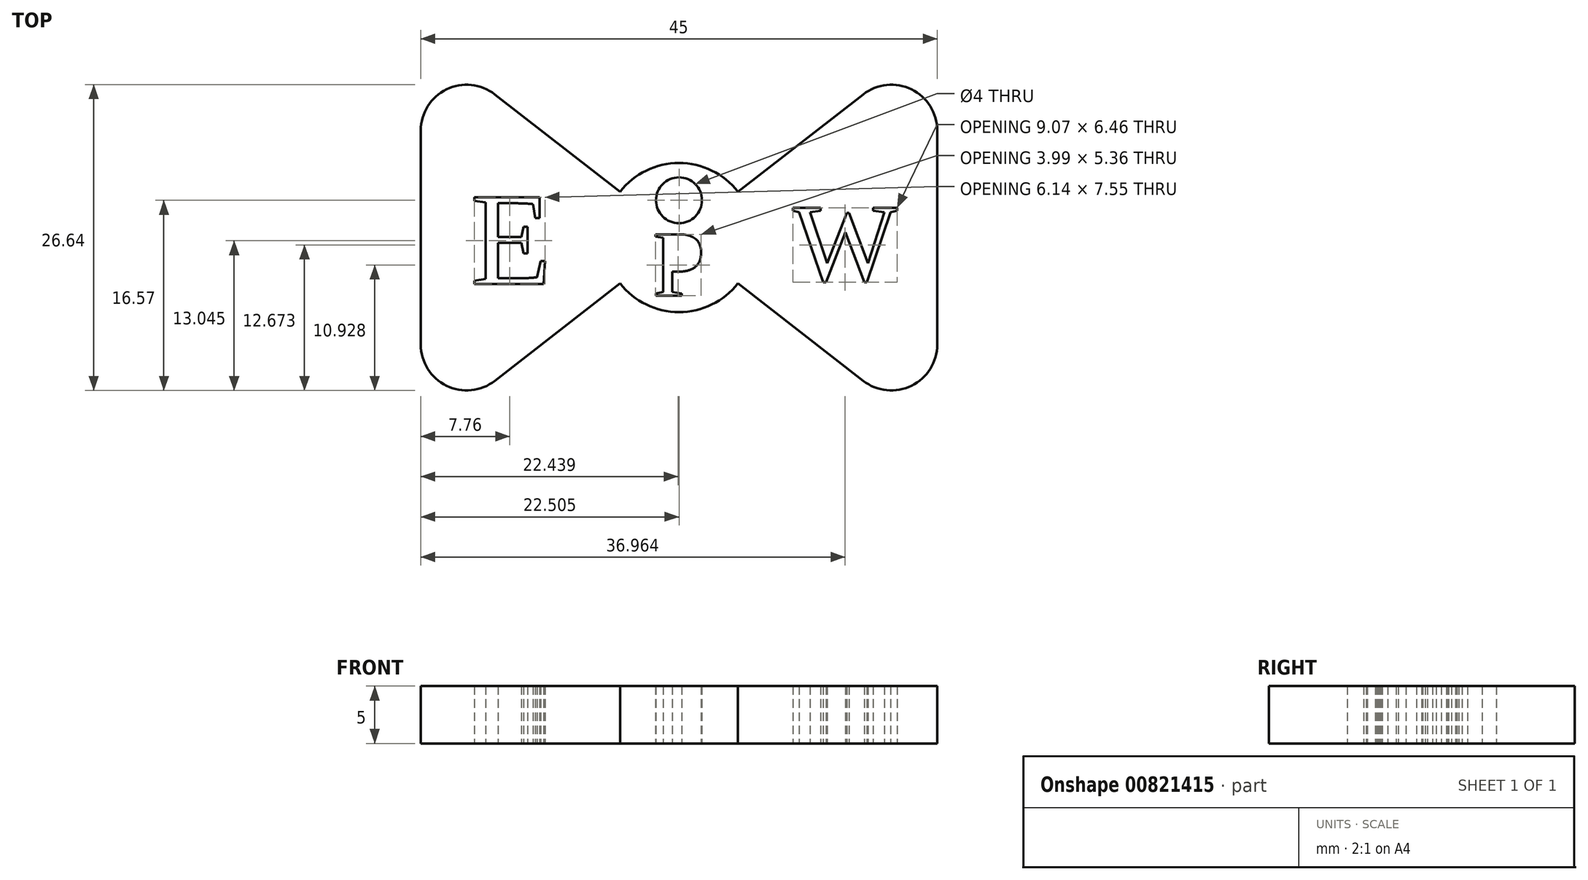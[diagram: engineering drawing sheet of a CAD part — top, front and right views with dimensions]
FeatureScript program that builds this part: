
annotation { "Feature Type Name" : "Feature", "Feature Type Description" : "" }
export const myFeature = defineFeature(function(context is Context, id is Id, definition is map)
    precondition{}
    {
        {
            var Q0;
            Q0=qCreatedBy(makeId("Top.planeOp"),FACE);
            var sketch = newSketch(context, id + "F0", { "sketchPlane" : qUnion([Q0])});
            skLineSegment(sketch, "E0", {"start": v(-32.88, -9.32) * mm, "end": v(-32.88, 9.32) * mm});
            skLineSegment(sketch, "E1", {"start": v(12.12, 9.32) * mm, "end": v(12.12, -9.32) * mm});
            skPoint(sketch, "E2.visualSharp", {"position": v(-32.88, 17.5) * mm});
            skArc(sketch, "E2.filletArc", {"start": v(-26.42, 12.48) * mm, "mid": v(-30.63, 12.91) * mm, "end": v(-32.88, 9.32) * mm});
            skPoint(sketch, "E3.visualSharp", {"position": v(-32.88, -17.5) * mm});
            skArc(sketch, "E3.filletArc", {"start": v(-32.88, -9.32) * mm, "mid": v(-30.63, -12.91) * mm, "end": v(-26.42, -12.48) * mm});
            skPoint(sketch, "E4.visualSharp", {"position": v(12.12, -17.5) * mm});
            skArc(sketch, "E4.filletArc", {"start": v(5.67, -12.48) * mm, "mid": v(9.88, -12.91) * mm, "end": v(12.12, -9.32) * mm});
            skPoint(sketch, "E5.visualSharp", {"position": v(12.12, 17.5) * mm});
            skArc(sketch, "E5.filletArc", {"start": v(12.12, 9.32) * mm, "mid": v(9.88, 12.91) * mm, "end": v(5.67, 12.48) * mm});
            skCircle(sketch, "E6", {"center": v(-10.38, 0) * mm, "radius": 6.5 * mm});
            skLineSegment(sketch, "E7", {"start": v(-26.42, -12.48) * mm, "end": v(-15.5, -4) * mm});
            skLineSegment(sketch, "E8", {"start": v(-26.42, 12.48) * mm, "end": v(-15.5, 4) * mm});
            skLineSegment(sketch, "E9", {"start": v(-5.24, 4) * mm, "end": v(5.67, 12.48) * mm});
            skLineSegment(sketch, "E10", {"start": v(-5.24, -4) * mm, "end": v(5.67, -12.48) * mm});
            skText(sketch, "E11", { "text": "E", "fontName": "Tinos-Regular.ttf"});
            skText(sketch, "E12", { "text": "W", "fontName": "Tinos-Regular.ttf"});
            skText(sketch, "E13", { "text": "P", "fontName": "Tinos-Regular.ttf"});
            skCircle(sketch, "E14", {"center": v(-10.38, 3.25) * mm, "radius": 2 * mm});
            const initialGuessF0  = {"E11": [-0.02852, -0.00405, 1, 0, 0.0083], "E12": [-0.00046, -0.00373, 1, 0, 0.00694], "E13": [-0.01267, -0.00507, 1, 0, 0.00589]};
            skSetInitialGuess(sketch, initialGuessF0);
            skSolve(sketch);
        }
        {
            var Q0;
            Q0=makeQuery(id+"F0.imprint","IMPRINT",FACE,{"disambiguationData":[TD([[makeQuery(id+"F0.imprint","IMPRINT",EDGE,{"derivedFrom":sQuery(id+"F0.wireOp",EDGE,"E1")}),-1.0]])]});
            var Q1;
            Q1=makeQuery(id+"F0.imprint","IMPRINT",FACE,{"disambiguationData":[TD([[makeQuery(id+"F0.imprint","IMPRINT",EDGE,{"derivedFrom":sQuery(id+"F0.wireOp",EDGE,"E13.sketch_text.stroke-7")}),1.0]])]});
            var Q2;
            Q2=makeQuery(id+"F0.imprint","IMPRINT",FACE,{"disambiguationData":[TD([[makeQuery(id+"F0.imprint","IMPRINT",EDGE,{"derivedFrom":sQuery(id+"F0.wireOp",EDGE,"E0")}),-1.0]])]});
            extrude(context, id + "F1", {"entities" : qUnion([Q0, Q1, Q2]), "depth" : 5 * mm, "offsetDistance" : 25 * mm});
        }
    });
